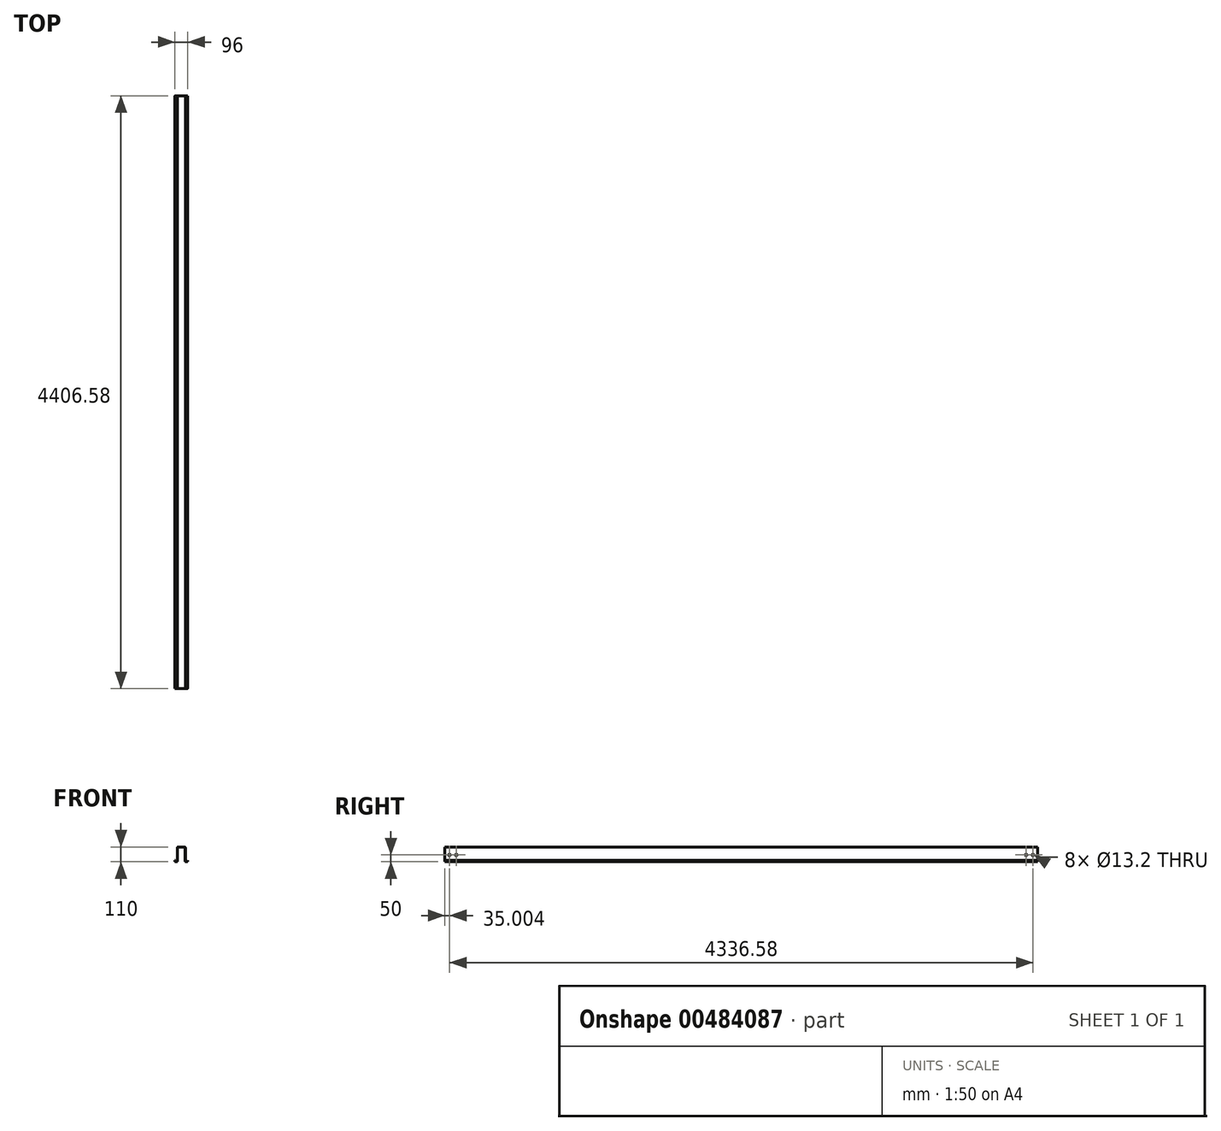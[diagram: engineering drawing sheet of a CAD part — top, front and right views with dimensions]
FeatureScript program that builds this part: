
annotation { "Feature Type Name" : "Feature", "Feature Type Description" : "" }
export const myFeature = defineFeature(function(context is Context, id is Id, definition is map)
    precondition{}
    {
        {
            var Q0;
            Q0=qCreatedBy(makeId("Front.planeOp"),FACE);
            var sketch = newSketch(context, id + "F0", { "sketchPlane" : qUnion([Q0])});
            skLineSegment(sketch, "E0", {"start": v(0, 0) * mm, "end": v(0, -3) * mm});
            skLineSegment(sketch, "E1", {"start": v(5, -8) * mm, "end": v(11, -8) * mm});
            skLineSegment(sketch, "E2", {"start": v(16, -3) * mm, "end": v(16, 95) * mm});
            skLineSegment(sketch, "E3", {"start": v(21, 100) * mm, "end": v(71, 100) * mm});
            skLineSegment(sketch, "E4", {"start": v(76, 95) * mm, "end": v(76, -3) * mm});
            skLineSegment(sketch, "E5", {"start": v(81, -8) * mm, "end": v(87, -8) * mm});
            skLineSegment(sketch, "E6", {"start": v(92, -3) * mm, "end": v(92, 0) * mm});
            skLineSegment(sketch, "E7", {"start": v(92, 0) * mm, "end": v(94, 0) * mm});
            skLineSegment(sketch, "E8", {"start": v(94, 0) * mm, "end": v(94, -5) * mm});
            skLineSegment(sketch, "E9", {"start": v(89, -10) * mm, "end": v(79, -10) * mm});
            skLineSegment(sketch, "E10", {"start": v(74, -5) * mm, "end": v(74, 93) * mm});
            skLineSegment(sketch, "E11", {"start": v(69, 98) * mm, "end": v(23, 98) * mm});
            skLineSegment(sketch, "E12", {"start": v(18, 93) * mm, "end": v(18, -5) * mm});
            skLineSegment(sketch, "E13", {"start": v(13, -10) * mm, "end": v(3, -10) * mm});
            skLineSegment(sketch, "E14", {"start": v(-2, -5) * mm, "end": v(-2, 0) * mm});
            skLineSegment(sketch, "E15", {"start": v(-2, 0) * mm, "end": v(0, 0) * mm});
            skPoint(sketch, "E16.visualSharp", {"position": v(18, 98) * mm});
            skArc(sketch, "E16.filletArc", {"start": v(23, 98) * mm, "mid": v(19.46, 96.54) * mm, "end": v(18, 93) * mm});
            skPoint(sketch, "E17.visualSharp", {"position": v(74, 98) * mm});
            skArc(sketch, "E17.filletArc", {"start": v(74, 93) * mm, "mid": v(72.54, 96.54) * mm, "end": v(69, 98) * mm});
            skPoint(sketch, "E18.visualSharp", {"position": v(16, 100) * mm});
            skArc(sketch, "E18.filletArc", {"start": v(21, 100) * mm, "mid": v(17.46, 98.54) * mm, "end": v(16, 95) * mm});
            skPoint(sketch, "E19.visualSharp", {"position": v(76, 100) * mm});
            skArc(sketch, "E19.filletArc", {"start": v(76, 95) * mm, "mid": v(74.54, 98.54) * mm, "end": v(71, 100) * mm});
            skPoint(sketch, "E20.visualSharp", {"position": v(74, -10) * mm});
            skArc(sketch, "E20.filletArc", {"start": v(74, -5) * mm, "mid": v(75.46, -8.54) * mm, "end": v(79, -10) * mm});
            skPoint(sketch, "E21.visualSharp", {"position": v(76, -8) * mm});
            skArc(sketch, "E21.filletArc", {"start": v(76, -3) * mm, "mid": v(77.46, -6.54) * mm, "end": v(81, -8) * mm});
            skPoint(sketch, "E22.visualSharp", {"position": v(92, -8) * mm});
            skArc(sketch, "E22.filletArc", {"start": v(87, -8) * mm, "mid": v(90.54, -6.54) * mm, "end": v(92, -3) * mm});
            skPoint(sketch, "E23.visualSharp", {"position": v(94, -10) * mm});
            skArc(sketch, "E23.filletArc", {"start": v(89, -10) * mm, "mid": v(92.54, -8.54) * mm, "end": v(94, -5) * mm});
            skPoint(sketch, "E24.visualSharp", {"position": v(18, -10) * mm});
            skArc(sketch, "E24.filletArc", {"start": v(13, -10) * mm, "mid": v(16.54, -8.54) * mm, "end": v(18, -5) * mm});
            skPoint(sketch, "E25.visualSharp", {"position": v(16, -8) * mm});
            skArc(sketch, "E25.filletArc", {"start": v(11, -8) * mm, "mid": v(14.54, -6.54) * mm, "end": v(16, -3) * mm});
            skPoint(sketch, "E26.visualSharp", {"position": v(-2, -10) * mm});
            skArc(sketch, "E26.filletArc", {"start": v(-2, -5) * mm, "mid": v(-0.54, -8.54) * mm, "end": v(3, -10) * mm});
            skPoint(sketch, "E27.visualSharp", {"position": v(0, -8) * mm});
            skArc(sketch, "E27.filletArc", {"start": v(0, -3) * mm, "mid": v(1.46, -6.54) * mm, "end": v(5, -8) * mm});
            skSolve(sketch);
        }
        {
            var Q0;
            Q0 = qSketchRegion(id + "F0", true);
            extrude(context, id + "F1", {"entities" : qUnion([Q0]), "depth" : 4406.58 * mm});
        }
        {
            var Q0;
            Q0=makeQuery(id+"F1.opExtrude","SWEPT_FACE",FACE,{"disambiguationData":[OSD([sQuery(id+"F0.wireOp",EDGE,"E4")])]});
            var sketch = newSketch(context, id + "F2", { "sketchPlane" : qUnion([Q0])});
            skLineSegment(sketch, "E28", {"start": v(0, 46) * mm, "end": v(-35, 46) * mm});
            skLineSegment(sketch, "E29", {"start": v(-35, 46) * mm, "end": v(-85, 46) * mm});
            skLineSegment(sketch, "E30", {"start": v(-4406.58, 46) * mm, "end": v(-4371.58, 46) * mm});
            skLineSegment(sketch, "E31", {"start": v(-4371.58, 46) * mm, "end": v(-4321.58, 46) * mm});
            skLineSegment(sketch, "E32", {"start": v(-85, 46) * mm, "end": v(-85, 40) * mm});
            skLineSegment(sketch, "E33", {"start": v(-35, 46) * mm, "end": v(-35, 40) * mm});
            skLineSegment(sketch, "E34", {"start": v(-4371.58, 46) * mm, "end": v(-4371.58, 40) * mm});
            skLineSegment(sketch, "E35", {"start": v(-4321.58, 46) * mm, "end": v(-4321.58, 40) * mm});
            skSolve(sketch);
        }
        {
            var Q0;
            Q0=sQuery(id+"F2.wireOp",VERTEX,"E34.end");
            var Q1;
            Q1=sQuery(id+"F2.wireOp",VERTEX,"E35.end");
            var Q2;
            Q2=sQuery(id+"F2.wireOp",VERTEX,"E32.end");
            var Q3;
            Q3=sQuery(id+"F2.wireOp",VERTEX,"E33.end");
            var Q4;
            Q4=makeQuery(id+"F1.opExtrude","SWEPT_BODY",BODY,{"disambiguationData":[OSD([sQuery(id+"F0.wireOp",EDGE,"E0"),sQuery(id+"F0.wireOp",EDGE,"E1"),sQuery(id+"F0.wireOp",EDGE,"E2"),sQuery(id+"F0.wireOp",EDGE,"E3"),sQuery(id+"F0.wireOp",EDGE,"E4"),sQuery(id+"F0.wireOp",EDGE,"E5"),sQuery(id+"F0.wireOp",EDGE,"E6"),sQuery(id+"F0.wireOp",EDGE,"E7"),sQuery(id+"F0.wireOp",EDGE,"E8"),sQuery(id+"F0.wireOp",EDGE,"E9"),sQuery(id+"F0.wireOp",EDGE,"E10"),sQuery(id+"F0.wireOp",EDGE,"E11"),sQuery(id+"F0.wireOp",EDGE,"E12"),sQuery(id+"F0.wireOp",EDGE,"E13"),sQuery(id+"F0.wireOp",EDGE,"E14"),sQuery(id+"F0.wireOp",EDGE,"E15"),sQuery(id+"F0.wireOp",EDGE,"E16.filletArc"),sQuery(id+"F0.wireOp",EDGE,"E17.filletArc"),sQuery(id+"F0.wireOp",EDGE,"E18.filletArc"),sQuery(id+"F0.wireOp",EDGE,"E19.filletArc"),sQuery(id+"F0.wireOp",EDGE,"E20.filletArc"),sQuery(id+"F0.wireOp",EDGE,"E21.filletArc"),sQuery(id+"F0.wireOp",EDGE,"E22.filletArc"),sQuery(id+"F0.wireOp",EDGE,"E23.filletArc"),sQuery(id+"F0.wireOp",EDGE,"E24.filletArc"),sQuery(id+"F0.wireOp",EDGE,"E25.filletArc"),sQuery(id+"F0.wireOp",EDGE,"E26.filletArc"),sQuery(id+"F0.wireOp",EDGE,"E27.filletArc")])]});
            hole(context, id + "F3", {"style" : HoleStyle.SIMPLE, "endStyle" : HoleEndStyle.THROUGH, "standardTappedOrClearance" : lookupTablePath({ "standard" : "ISO", "fit" : "Normal", "size" : "M12", "type" : "Clearance" }), "standardBlindInLast" : lookupTablePath({ "fit" : "Standard", "standard" : "ISO", "size" : "M12", "type" : "Clearance" }), "holeDiameter" : 13.2 * mm, "isTappedThrough" : true, "tappedDepth" : 12 * mm, "tapClearance" : 3, "locations" : qUnion([Q0, Q1, Q2, Q3]), "scope" : qUnion([Q4])});
        }
    });
